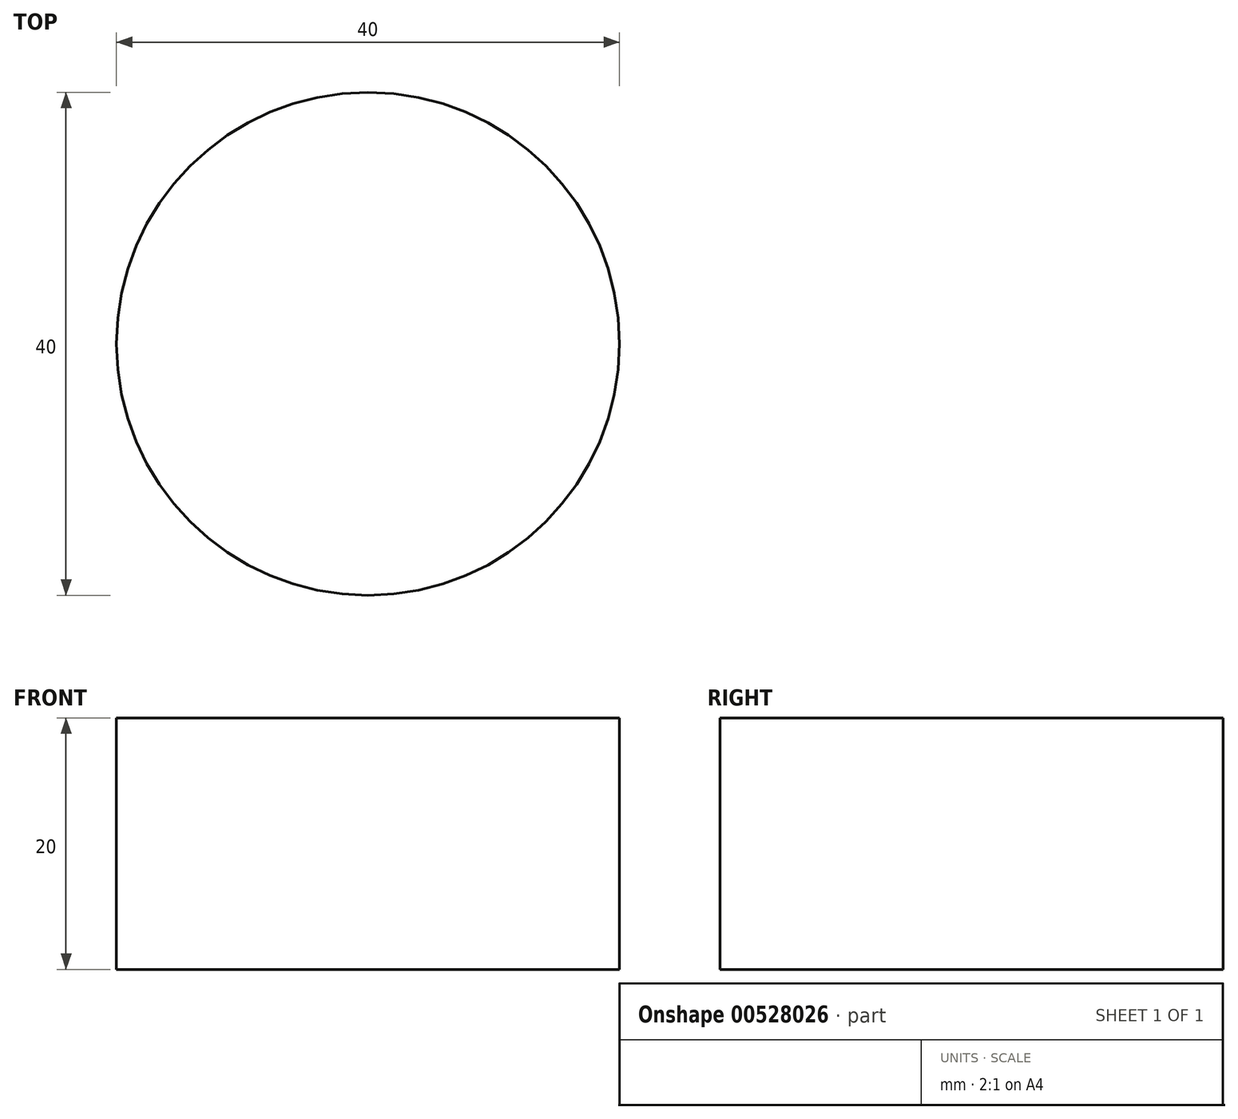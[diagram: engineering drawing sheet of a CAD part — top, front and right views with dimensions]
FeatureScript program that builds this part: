
annotation { "Feature Type Name" : "Feature", "Feature Type Description" : "" }
export const myFeature = defineFeature(function(context is Context, id is Id, definition is map)
    precondition{}
    {
        {
            var Q0;
            Q0=qCreatedBy(makeId("Top.planeOp"),FACE);
            var sketch = newSketch(context, id + "F0", { "sketchPlane" : qUnion([Q0])});
            skCircle(sketch, "E0", {"center": v(0, 0) * mm, "radius": 20 * mm});
            skSolve(sketch);
        }
        {
            var Q0;
            Q0=makeQuery(id+"F0.imprint","IMPRINT",FACE,{"disambiguationData":[TD([[makeQuery(id+"F0.imprint","IMPRINT",EDGE,{"derivedFrom":sQuery(id+"F0.wireOp",EDGE,"E0")}),1.0]])]});
            extrude(context, id + "F1", {"entities" : qUnion([Q0]), "depth" : 20 * mm, "offsetDistance" : 25 * mm});
        }
    });
